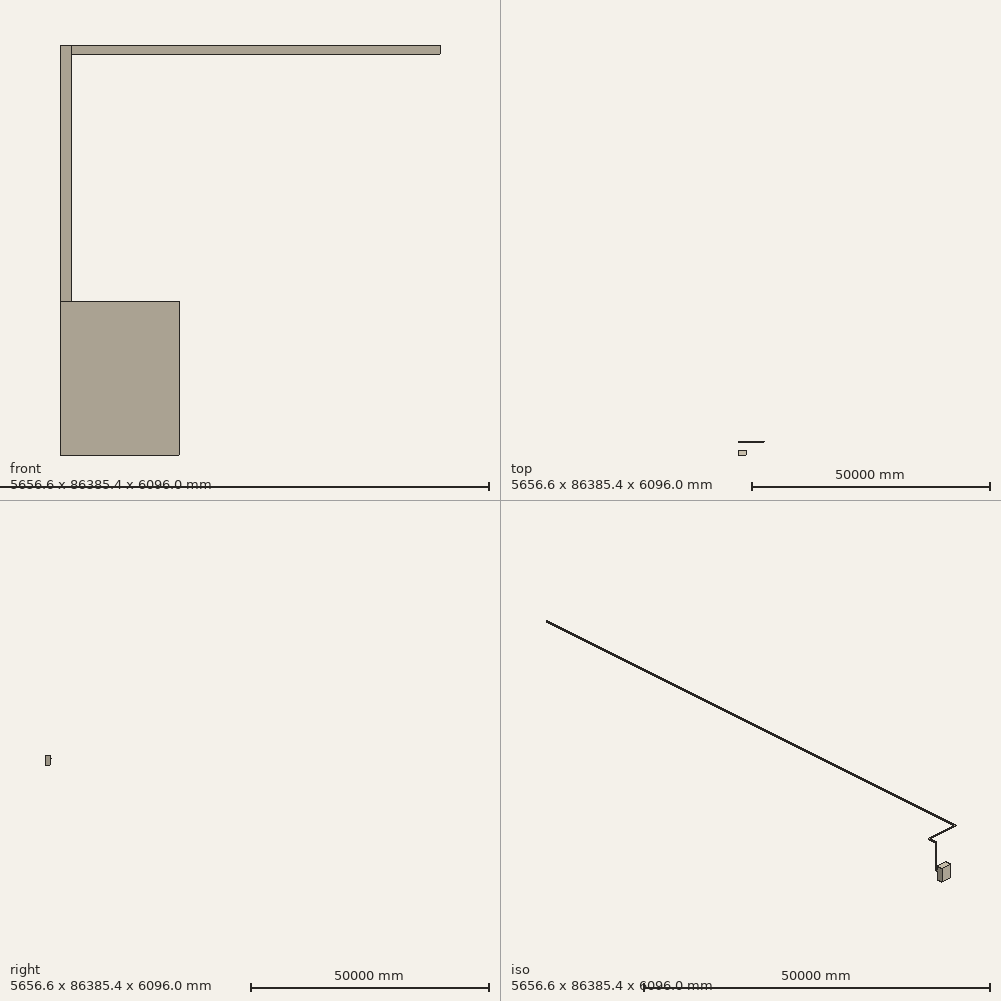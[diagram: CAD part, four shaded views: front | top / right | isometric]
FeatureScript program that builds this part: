
annotation { "Feature Type Name" : "Feature", "Feature Type Description" : "" }
export const myFeature = defineFeature(function(context is Context, id is Id, definition is map)
    precondition{}
    {
        {
            var Q0;
            Q0=qCreatedBy(makeId("Top.planeOp"),FACE);
            var sketch = newSketch(context, id + "F0", { "sketchPlane" : qUnion([Q0])});
            skLineSegment(sketch, "E0.bottom", {"start": v(0, 0) * mm, "end": v(1778, 0) * mm});
            skLineSegment(sketch, "E0.top", {"start": v(0, 965.2) * mm, "end": v(1778, 965.2) * mm});
            skLineSegment(sketch, "E0.left", {"start": v(0, 0) * mm, "end": v(0, 965.2) * mm});
            skLineSegment(sketch, "E0.right", {"start": v(1778, 0) * mm, "end": v(1778, 965.2) * mm});
            skSolve(sketch);
        }
        {
            var Q0;
            Q0=makeQuery(id+"F0.imprint","IMPRINT",FACE,{"disambiguationData":[TD([[makeQuery(id+"F0.imprint","IMPRINT",EDGE,{"derivedFrom":sQuery(id+"F0.wireOp",EDGE,"E0.bottom")}),1.0]])]});
            extrude(context, id + "F1", {"entities" : qUnion([Q0]), "depth" : 2286 * mm, "offsetDistance" : 25.4 * mm});
        }
        {
            var Q0;
            Q0=qCreatedBy(makeId("Top.planeOp"),FACE);
            var sketch = newSketch(context, id + "F2", { "sketchPlane" : qUnion([Q0])});
            skLineSegment(sketch, "E1.bottom", {"start": v(0, 0) * mm, "end": v(170.18, 0) * mm});
            skLineSegment(sketch, "E1.top", {"start": v(0, 127) * mm, "end": v(170.18, 127) * mm});
            skLineSegment(sketch, "E1.left", {"start": v(0, 0) * mm, "end": v(0, 127) * mm});
            skLineSegment(sketch, "E1.right", {"start": v(170.18, 0) * mm, "end": v(170.18, 127) * mm});
            skSolve(sketch);
        }
        {
            var Q0;
            Q0=makeQuery(id+"F2.imprint","IMPRINT",FACE,{"disambiguationData":[TD([[makeQuery(id+"F2.imprint","IMPRINT",EDGE,{"derivedFrom":sQuery(id+"F2.wireOp",EDGE,"E1.bottom")}),1.0]])]});
            extrude(context, id + "F3", {"entities" : qUnion([Q0]), "depth" : 1524 * mm, "offsetDistance" : 25.4 * mm});
        }
        {
            var Q0;
            Q0=makeQuery(id+"F3.opExtrude","SWEPT_FACE",FACE,{"disambiguationData":[OSD([sQuery(id+"F2.wireOp",EDGE,"E1.top")])]});
            var sketch = newSketch(context, id + "F4", { "sketchPlane" : qUnion([Q0])});
            skLineSegment(sketch, "E2.bottom", {"start": v(-170.18, 1524) * mm, "end": v(0, 1524) * mm});
            skLineSegment(sketch, "E2.top", {"start": v(-170.18, 1397) * mm, "end": v(0, 1397) * mm});
            skLineSegment(sketch, "E2.left", {"start": v(-170.18, 1524) * mm, "end": v(-170.18, 1397) * mm});
            skLineSegment(sketch, "E2.right", {"start": v(0, 1524) * mm, "end": v(0, 1397) * mm});
            skSolve(sketch);
        }
        {
            var Q0;
            Q0=makeQuery(id+"F4.imprint","IMPRINT",FACE,{"disambiguationData":[TD([[makeQuery(id+"F4.imprint","IMPRINT",EDGE,{"derivedFrom":sQuery(id+"F4.wireOp",EDGE,"E2.bottom")}),1.0]])]});
            extrude(context, id + "F5", {"entities" : qUnion([Q0]), "operationType" : NewBodyOperationType.ADD, "depth" : 1219.2 * mm, "offsetDistance" : 25.4 * mm});
        }
        {
            var Q0;
            Q0=makeQuery(id+"F5.boolean.opBoolean","MERGE",FACE,{"derivedFrom":[makeQuery(id+"F3.opExtrude","CAP_FACE",FACE,{"disambiguationData":[OSD([sQuery(id+"F2.wireOp",EDGE,"E1.bottom"),sQuery(id+"F2.wireOp",EDGE,"E1.top"),sQuery(id+"F2.wireOp",EDGE,"E1.left"),sQuery(id+"F2.wireOp",EDGE,"E1.right")])],"isStart":false}),makeQuery(id+"F5.opExtrude","SWEPT_FACE",FACE,{"disambiguationData":[OSD([sQuery(id+"F4.wireOp",EDGE,"E2.bottom")])]})]});
            var sketch = newSketch(context, id + "F6", { "sketchPlane" : qUnion([Q0])});
            skLineSegment(sketch, "E3.bottom", {"start": v(170.18, 1346.2) * mm, "end": v(0, 1346.2) * mm});
            skLineSegment(sketch, "E3.top", {"start": v(170.18, 1219.2) * mm, "end": v(0, 1219.2) * mm});
            skLineSegment(sketch, "E3.left", {"start": v(170.18, 1346.2) * mm, "end": v(170.18, 1219.2) * mm});
            skLineSegment(sketch, "E3.right", {"start": v(0, 1346.2) * mm, "end": v(0, 1219.2) * mm});
            skSolve(sketch);
        }
        {
            var Q0;
            Q0=makeQuery(id+"F6.imprint","IMPRINT",FACE,{"disambiguationData":[TD([[makeQuery(id+"F6.imprint","IMPRINT",EDGE,{"derivedFrom":sQuery(id+"F6.wireOp",EDGE,"E3.bottom")}),-1.0]])]});
            extrude(context, id + "F7", {"entities" : qUnion([Q0]), "operationType" : NewBodyOperationType.ADD, "depth" : 4572 * mm, "offsetDistance" : 25.4 * mm});
        }
        {
            var Q0;
            Q0=makeQuery(id+"F7.boolean.opBoolean","MERGE",FACE,{"derivedFrom":[makeQuery(id+"F5.opExtrude","CAP_FACE",FACE,{"disambiguationData":[OSD([sQuery(id+"F4.wireOp",EDGE,"E2.bottom"),sQuery(id+"F4.wireOp",EDGE,"E2.top"),sQuery(id+"F4.wireOp",EDGE,"E2.left"),sQuery(id+"F4.wireOp",EDGE,"E2.right")])],"isStart":false}),makeQuery(id+"F7.opExtrude","SWEPT_FACE",FACE,{"disambiguationData":[OSD([sQuery(id+"F6.wireOp",EDGE,"E3.bottom")])]})]});
            var sketch = newSketch(context, id + "F8", { "sketchPlane" : qUnion([Q0])});
            skLineSegment(sketch, "E4.bottom", {"start": v(-170.18, 6096) * mm, "end": v(0, 6096) * mm});
            skLineSegment(sketch, "E4.top", {"start": v(-170.18, 5969) * mm, "end": v(0, 5969) * mm});
            skLineSegment(sketch, "E4.left", {"start": v(-170.18, 6096) * mm, "end": v(-170.18, 5969) * mm});
            skLineSegment(sketch, "E4.right", {"start": v(0, 6096) * mm, "end": v(0, 5969) * mm});
            skSolve(sketch);
        }
        {
            var Q0;
            Q0=makeQuery(id+"F8.imprint","IMPRINT",FACE,{"disambiguationData":[TD([[makeQuery(id+"F8.imprint","IMPRINT",EDGE,{"derivedFrom":sQuery(id+"F8.wireOp",EDGE,"E4.bottom")}),1.0]])]});
            extrude(context, id + "F9", {"entities" : qUnion([Q0]), "operationType" : NewBodyOperationType.ADD, "depth" : 1524 * mm, "offsetDistance" : 25.4 * mm});
        }
        {
            var Q0;
            Q0=makeQuery(id+"F9.boolean.opBoolean","MERGE",FACE,{"derivedFrom":[makeQuery(id+"F7.boolean.opBoolean","MERGE",FACE,{"derivedFrom":[makeQuery(id+"F5.boolean.opBoolean","MERGE",FACE,{"derivedFrom":[makeQuery(id+"F3.opExtrude","SWEPT_FACE",FACE,{"disambiguationData":[OSD([sQuery(id+"F2.wireOp",EDGE,"E1.right")])]}),makeQuery(id+"F5.opExtrude","SWEPT_FACE",FACE,{"disambiguationData":[OSD([sQuery(id+"F4.wireOp",EDGE,"E2.left")])]})]}),makeQuery(id+"F7.opExtrude","SWEPT_FACE",FACE,{"disambiguationData":[OSD([sQuery(id+"F6.wireOp",EDGE,"E3.left")])]})]}),makeQuery(id+"F9.opExtrude","SWEPT_FACE",FACE,{"disambiguationData":[OSD([sQuery(id+"F8.wireOp",EDGE,"E4.left")])]})]});
            var sketch = newSketch(context, id + "F10", { "sketchPlane" : qUnion([Q0])});
            skLineSegment(sketch, "E5.bottom", {"start": v(2870.2, 5969) * mm, "end": v(2700.02, 5969) * mm});
            skLineSegment(sketch, "E5.top", {"start": v(2870.2, 6096) * mm, "end": v(2700.02, 6096) * mm});
            skLineSegment(sketch, "E5.left", {"start": v(2870.2, 5969) * mm, "end": v(2870.2, 6096) * mm});
            skLineSegment(sketch, "E5.right", {"start": v(2700.02, 5969) * mm, "end": v(2700.02, 6096) * mm});
            skSolve(sketch);
        }
        {
            var Q0;
            Q0=makeQuery(id+"F10.imprint","IMPRINT",FACE,{"disambiguationData":[TD([[makeQuery(id+"F10.imprint","IMPRINT",EDGE,{"derivedFrom":sQuery(id+"F10.wireOp",EDGE,"E5.bottom")}),-1.0]])]});
            extrude(context, id + "F11", {"entities" : qUnion([Q0]), "operationType" : NewBodyOperationType.ADD, "depth" : 5486.4 * mm, "offsetDistance" : 25.4 * mm});
        }
        {
            var Q0;
            Q0=makeQuery(id+"F11.boolean.opBoolean","MERGE",FACE,{"derivedFrom":[makeQuery(id+"F9.opExtrude","CAP_FACE",FACE,{"disambiguationData":[OSD([sQuery(id+"F8.wireOp",EDGE,"E4.bottom"),sQuery(id+"F8.wireOp",EDGE,"E4.top"),sQuery(id+"F8.wireOp",EDGE,"E4.left"),sQuery(id+"F8.wireOp",EDGE,"E4.right")])],"isStart":false}),makeQuery(id+"F11.opExtrude","SWEPT_FACE",FACE,{"disambiguationData":[OSD([sQuery(id+"F10.wireOp",EDGE,"E5.left")])]})]});
            var sketch = newSketch(context, id + "F12", { "sketchPlane" : qUnion([Q0])});
            skLineSegment(sketch, "E6.bottom", {"start": v(-5656.58, 5969) * mm, "end": v(-5486.4, 5969) * mm});
            skLineSegment(sketch, "E6.top", {"start": v(-5656.58, 6096) * mm, "end": v(-5486.4, 6096) * mm});
            skLineSegment(sketch, "E6.left", {"start": v(-5656.58, 5969) * mm, "end": v(-5656.58, 6096) * mm});
            skLineSegment(sketch, "E6.right", {"start": v(-5486.4, 5969) * mm, "end": v(-5486.4, 6096) * mm});
            skSolve(sketch);
        }
        {
            var Q0;
            Q0=makeQuery(id+"F12.imprint","IMPRINT",FACE,{"disambiguationData":[TD([[makeQuery(id+"F12.imprint","IMPRINT",EDGE,{"derivedFrom":sQuery(id+"F12.wireOp",EDGE,"E6.bottom")}),1.0]])]});
            extrude(context, id + "F13", {"entities" : qUnion([Q0]), "operationType" : NewBodyOperationType.ADD, "depth" : 83515.2 * mm, "offsetDistance" : 25.4 * mm});
        }
    });
